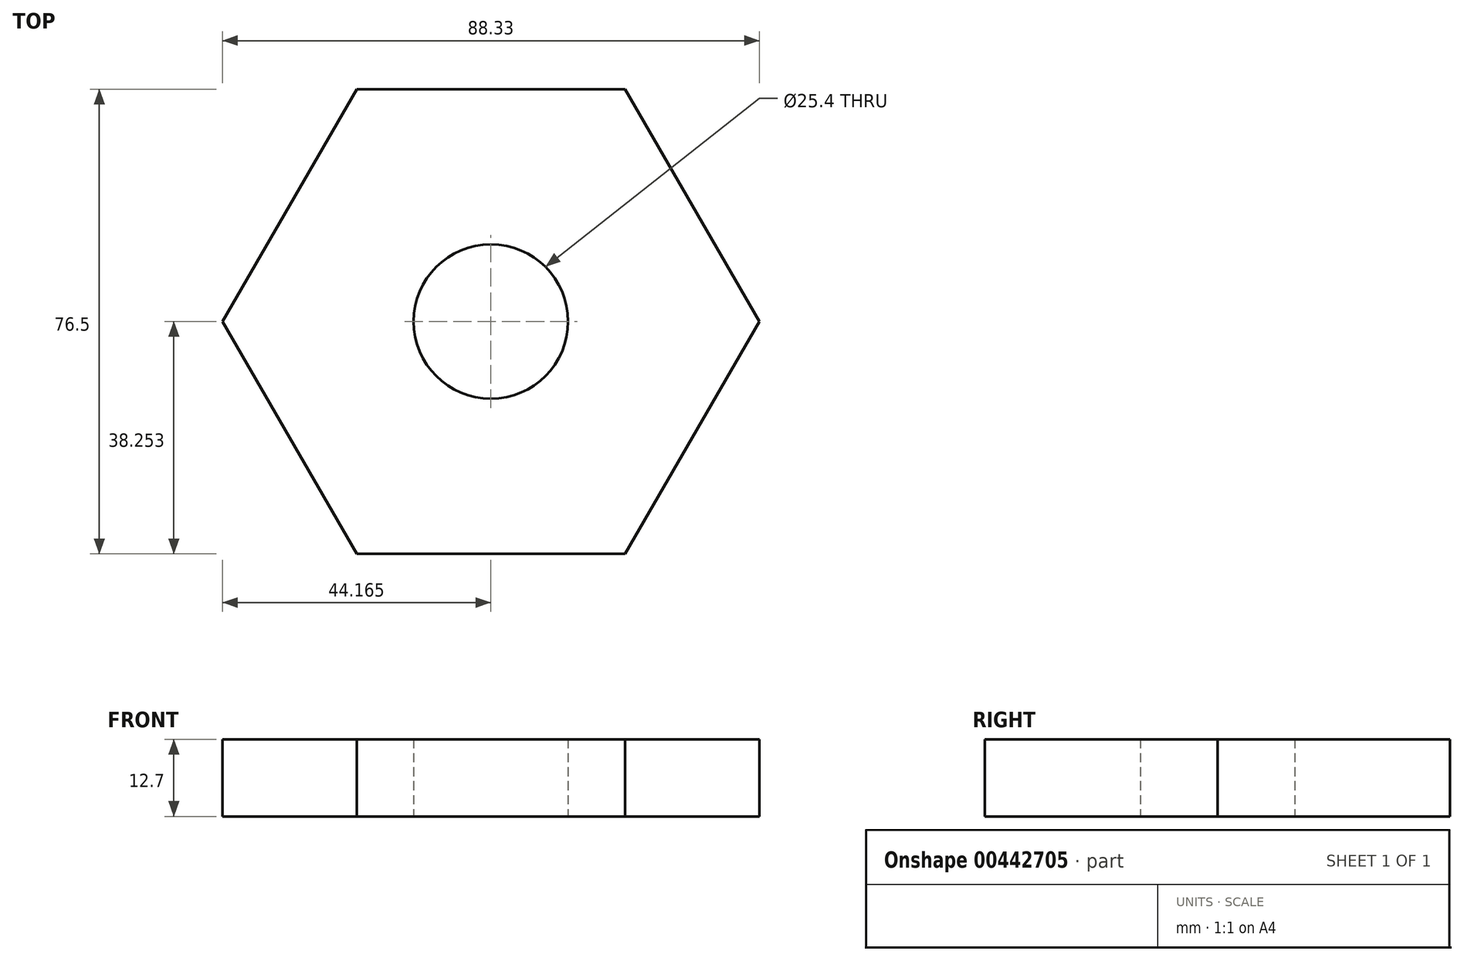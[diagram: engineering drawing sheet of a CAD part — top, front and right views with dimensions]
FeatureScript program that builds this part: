
annotation { "Feature Type Name" : "Feature", "Feature Type Description" : "" }
export const myFeature = defineFeature(function(context is Context, id is Id, definition is map)
    precondition{}
    {
        {
            var Q0;
            Q0=qCreatedBy(makeId("Top.planeOp"),FACE);
            var sketch = newSketch(context, id + "F0", { "sketchPlane" : qUnion([Q0])});
            skCircle(sketch, "E0.cCircle", {"center": v(-35.64, 37.53) * mm, "radius": 38.25 * mm, "construction": true});
            skLineSegment(sketch, "E0.0", {"start": v(-57.73, 75.78) * mm, "end": v(-13.56, 75.78) * mm});
            skLineSegment(sketch, "E0.1", {"start": v(-13.56, 75.78) * mm, "end": v(8.52, 37.53) * mm});
            skLineSegment(sketch, "E0.2", {"start": v(8.52, 37.53) * mm, "end": v(-13.56, -0.72) * mm});
            skLineSegment(sketch, "E0.3", {"start": v(-13.56, -0.72) * mm, "end": v(-57.73, -0.72) * mm});
            skLineSegment(sketch, "E0.4", {"start": v(-57.73, -0.72) * mm, "end": v(-79.81, 37.53) * mm});
            skLineSegment(sketch, "E0.5", {"start": v(-79.81, 37.53) * mm, "end": v(-57.73, 75.78) * mm});
            skPoint(sketch, "E0.0.midPoint", {"position": v(-35.64, 75.78) * mm});
            skCircle(sketch, "E1", {"center": v(-35.64, 37.53) * mm, "radius": 12.7 * mm});
            skSolve(sketch);
        }
        {
            var Q0;
            Q0=makeQuery(id+"F0.imprint","IMPRINT",FACE,{"disambiguationData":[TD([[makeQuery(id+"F0.imprint","IMPRINT",EDGE,{"derivedFrom":sQuery(id+"F0.wireOp",EDGE,"E0.0")}),-1.0]])]});
            extrude(context, id + "F1", {"entities" : qUnion([Q0]), "depth" : 12.7 * mm});
        }
    });
